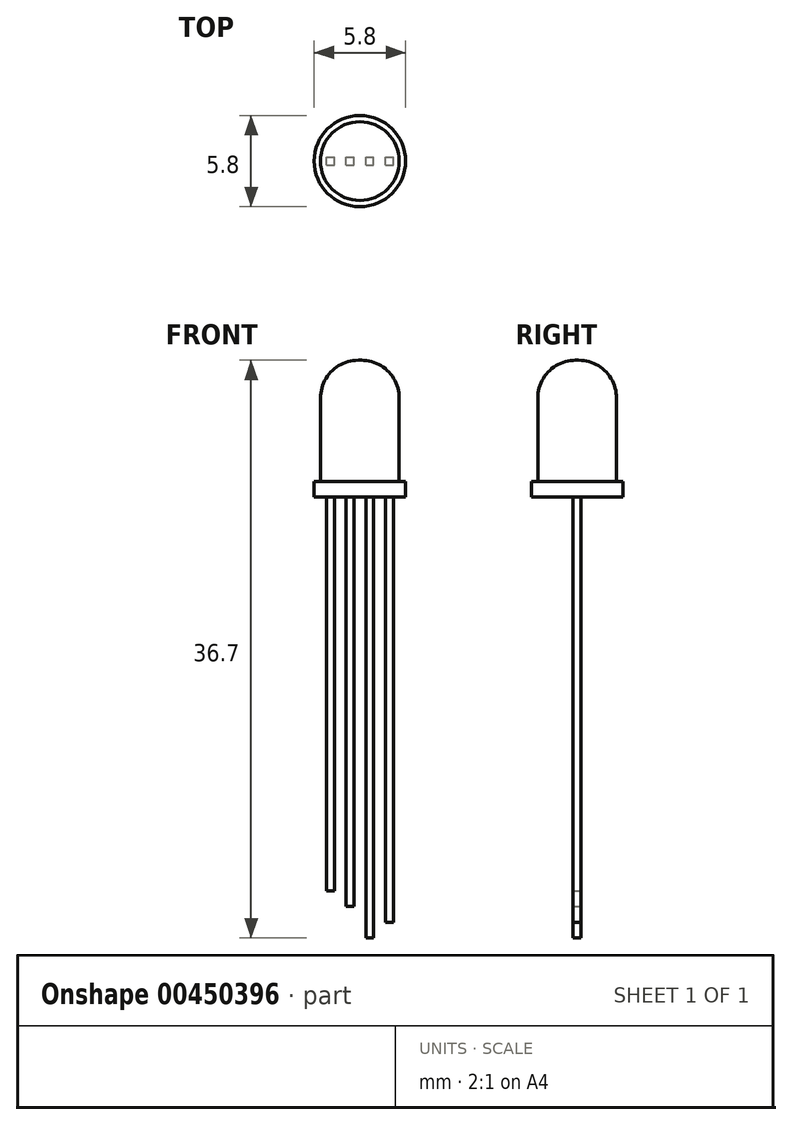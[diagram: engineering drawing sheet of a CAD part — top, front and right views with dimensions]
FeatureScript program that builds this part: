
annotation { "Feature Type Name" : "Feature", "Feature Type Description" : "" }
export const myFeature = defineFeature(function(context is Context, id is Id, definition is map)
    precondition{}
    {
        {
            var Q0;
            Q0=qCreatedBy(makeId("Top.planeOp"),FACE);
            var sketch = newSketch(context, id + "F0", { "sketchPlane" : qUnion([Q0])});
            skCircle(sketch, "E0", {"center": v(0, 0) * mm, "radius": 2.9 * mm});
            skSolve(sketch);
        }
        {
            var Q0;
            Q0=makeQuery(id+"F0.imprint","IMPRINT",FACE,{"disambiguationData":[TD([[makeQuery(id+"F0.imprint","IMPRINT",EDGE,{"derivedFrom":sQuery(id+"F0.wireOp",EDGE,"E0")}),1.0]])]});
            extrude(context, id + "F1", {"entities" : qUnion([Q0]), "depth" : 1 * mm});
        }
        {
            var Q0;
            Q0=qCreatedBy(makeId("Top.planeOp"),FACE);
            var sketch = newSketch(context, id + "F2", { "sketchPlane" : qUnion([Q0])});
            skCircle(sketch, "E1", {"center": v(0, 0) * mm, "radius": 2.5 * mm});
            skSolve(sketch);
        }
        {
            var Q0;
            Q0 = qSketchRegion(id + "F2", true);
            extrude(context, id + "F3", {"entities" : qUnion([Q0]), "operationType" : NewBodyOperationType.ADD, "depth" : 8.7 * mm});
        }
        {
            var Q0;
            Q0=makeQuery(id+"F3.opExtrude","CAP_EDGE",EDGE,{"disambiguationData":[OSD([sQuery(id+"F2.wireOp",EDGE,"E1")])],"isStart":false});
            fillet(context, id + "F4", {"entities" : qUnion([Q0]), "radius" : 2.4 * mm, "tangentPropagation" : true, "allowEdgeOverflow" : false});
        }
        {
            var Q0;
            Q0=qCreatedBy(makeId("Front.planeOp"),FACE);
            var sketch = newSketch(context, id + "F5", { "sketchPlane" : qUnion([Q0])});
            skLineSegment(sketch, "E2.bottom", {"start": v(-2.13, 0) * mm, "end": v(-1.63, 0) * mm});
            skLineSegment(sketch, "E2.top", {"start": v(-2.13, -25) * mm, "end": v(-1.63, -25) * mm});
            skLineSegment(sketch, "E2.left", {"start": v(-2.13, 0) * mm, "end": v(-2.13, -25) * mm});
            skLineSegment(sketch, "E2.right", {"start": v(-1.63, 0) * mm, "end": v(-1.63, -25) * mm});
            skLineSegment(sketch, "E3.bottom", {"start": v(-0.88, 0) * mm, "end": v(-0.37, 0) * mm});
            skLineSegment(sketch, "E3.top", {"start": v(-0.88, -26) * mm, "end": v(-0.38, -26) * mm});
            skLineSegment(sketch, "E3.left", {"start": v(-0.88, 0) * mm, "end": v(-0.88, -26) * mm});
            skLineSegment(sketch, "E3.right", {"start": v(-0.38, 0) * mm, "end": v(-0.38, -26) * mm});
            skLineSegment(sketch, "E4.bottom", {"start": v(0.38, 0) * mm, "end": v(0.87, 0) * mm});
            skLineSegment(sketch, "E4.top", {"start": v(0.37, -28) * mm, "end": v(0.87, -28) * mm});
            skLineSegment(sketch, "E4.left", {"start": v(0.37, 0) * mm, "end": v(0.37, -28) * mm});
            skLineSegment(sketch, "E4.right", {"start": v(0.87, 0) * mm, "end": v(0.87, -28) * mm});
            skLineSegment(sketch, "E5.bottom", {"start": v(1.62, 0) * mm, "end": v(2.12, 0) * mm});
            skLineSegment(sketch, "E5.top", {"start": v(1.62, -27) * mm, "end": v(2.12, -27) * mm});
            skLineSegment(sketch, "E5.left", {"start": v(1.62, 0) * mm, "end": v(1.62, -27) * mm});
            skLineSegment(sketch, "E5.right", {"start": v(2.12, 0) * mm, "end": v(2.12, -27) * mm});
            skSolve(sketch);
        }
        {
            var Q0;
            Q0 = qSketchRegion(id + "F5", true);
            extrude(context, id + "F6", {"entities" : qUnion([Q0]), "operationType" : NewBodyOperationType.ADD, "endBound" : BoundingType.SYMMETRIC, "depth" : .5 * mm});
        }
    });
